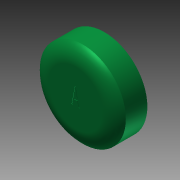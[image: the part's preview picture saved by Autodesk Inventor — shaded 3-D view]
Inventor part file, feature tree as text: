
AUTODESK INVENTOR PART (.ipt)
format: ipt  version: 2012 SP1 (Build 160190100, 190)  size: 117,248 bytes
history: native  units: in
note: dims shown in document units (in); Inventor stores cm internally (conversion verified against a paired STEP export)
features: extrude x2, sketch x2, chamfer x1, fillet x1
ambient origin geometry x8: Origin, YZ Plane, XZ Plane, XY Plane, X Axis, Y Axis, Z Axis, Center Point
bodies: Solid1 (feature_tree)
feature tree (6):
  extrude  "Extrusion1"  Depth=0.2in TaperAngle=0.0deg
  chamfer  "Chamfer1"  Distance=0.05in Angle=45.0deg
  fillet  "Fillet1"  Radius=0.15in
  extrude  "Extrusion2"  [1 undecoded]
  sketch  "Sketch1"  dims[d0=0.6in d1=0.2in d2=0.0in d3=0.05in d4=0.125in d5=45.0deg d6=0.15in]
  sketch  "Sketch2"  dims[d7=0.0025in d8=0.0in]
note: 1 required parameter value undecoded (feature->parameter linkage not recoverable at this tier; creation-order binding heuristic only, values carry confidence <= 0.55)
